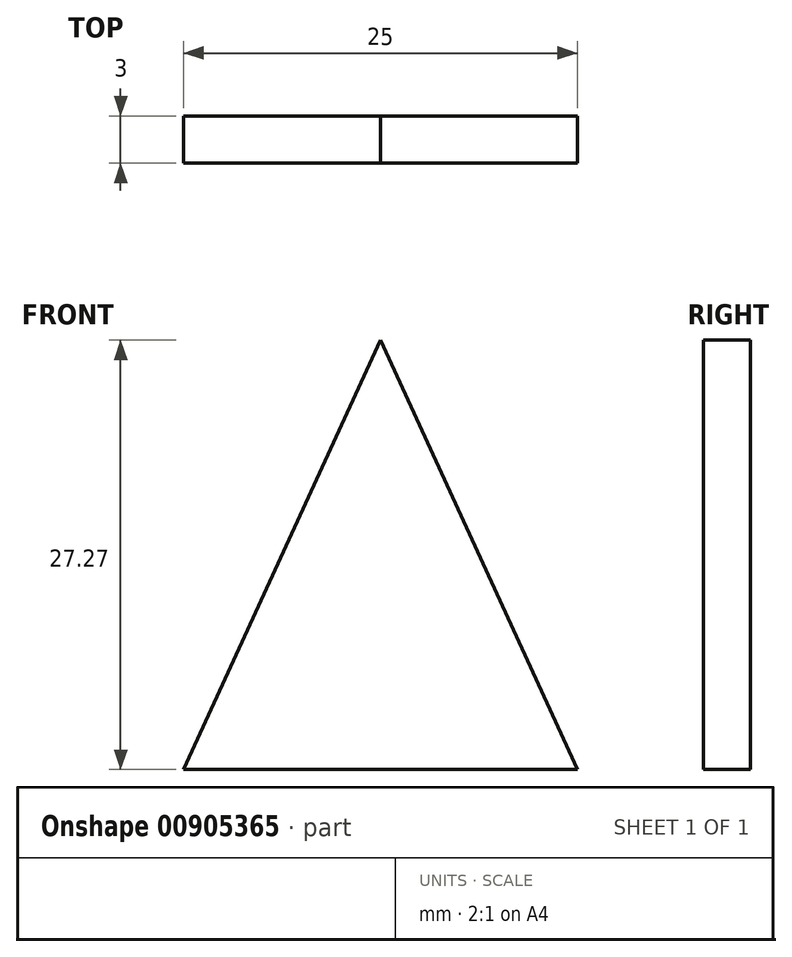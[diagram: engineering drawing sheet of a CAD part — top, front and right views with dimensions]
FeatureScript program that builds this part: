
annotation { "Feature Type Name" : "Feature", "Feature Type Description" : "" }
export const myFeature = defineFeature(function(context is Context, id is Id, definition is map)
    precondition{}
    {
        {
            var Q0;
            Q0=qCreatedBy(makeId("Front.planeOp"),FACE);
            var sketch = newSketch(context, id + "F0", { "sketchPlane" : qUnion([Q0])});
            skLineSegment(sketch, "E0", {"start": v(0, 27.27) * mm, "end": v(-12.5, 0) * mm});
            skLineSegment(sketch, "E1", {"start": v(-12.5, 0) * mm, "end": v(12.5, 0) * mm});
            skLineSegment(sketch, "E2", {"start": v(12.5, 0) * mm, "end": v(0, 27.27) * mm});
            skSolve(sketch);
        }
        {
            var Q0;
            Q0=makeQuery(id+"F0.imprint","IMPRINT",FACE,{"disambiguationData":[TD([[makeQuery(id+"F0.imprint","IMPRINT",EDGE,{"derivedFrom":sQuery(id+"F0.wireOp",EDGE,"E0")}),1.0]])]});
            extrude(context, id + "F1", {"entities" : qUnion([Q0]), "depth" : 3 * mm, "offsetDistance" : 25 * mm});
        }
    });
